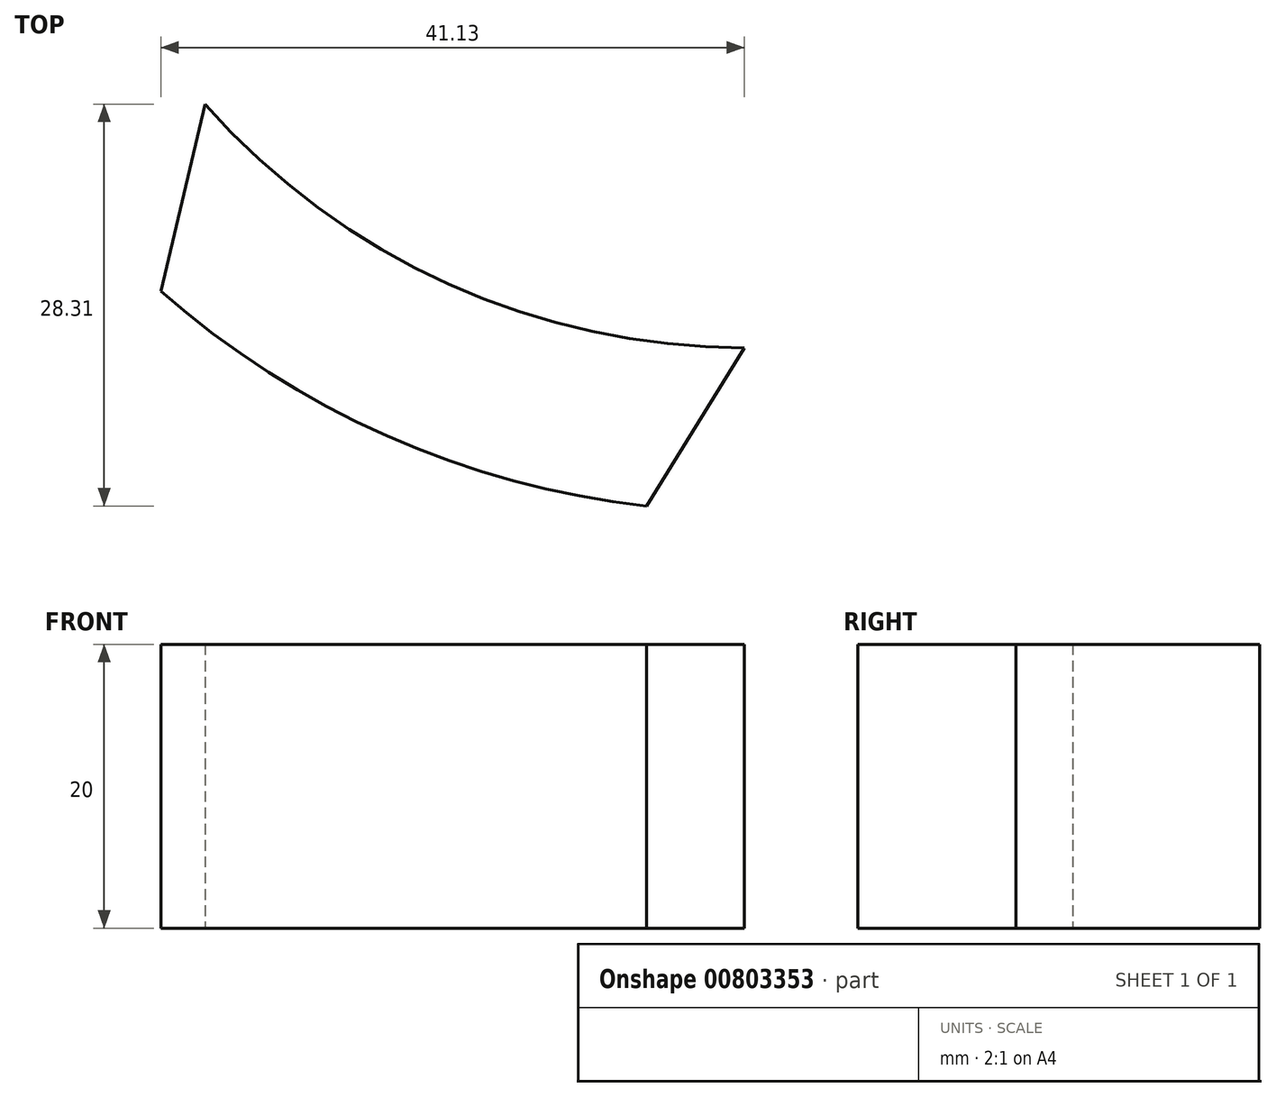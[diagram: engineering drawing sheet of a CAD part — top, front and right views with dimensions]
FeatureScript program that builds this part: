
annotation { "Feature Type Name" : "Feature", "Feature Type Description" : "" }
export const myFeature = defineFeature(function(context is Context, id is Id, definition is map)
    precondition{}
    {
        {
            var Q0;
            Q0=qCreatedBy(makeId("Top.planeOp"),FACE);
            var sketch = newSketch(context, id + "F0", { "sketchPlane" : qUnion([Q0])});
            skArc(sketch, "E0", {"start": v(-38.01, -33.51) * mm, "mid": v(-20.85, -46.19) * mm, "end": v(0, -50.68) * mm});
            skArc(sketch, "E1", {"start": v(-41.13, -46.67) * mm, "mid": v(-25.19, -56.88) * mm, "end": v(-6.9, -61.82) * mm});
            skLineSegment(sketch, "E2", {"start": v(-38.01, -33.51) * mm, "end": v(-41.13, -46.67) * mm});
            skLineSegment(sketch, "E3", {"start": v(0, -50.68) * mm, "end": v(-6.9, -61.82) * mm});
            skSolve(sketch);
        }
        {
            var Q0;
            Q0=makeQuery(id+"F0.imprint","IMPRINT",FACE,{"disambiguationData":[TD([[makeQuery(id+"F0.imprint","IMPRINT",EDGE,{"derivedFrom":sQuery(id+"F0.wireOp",EDGE,"E0")}),-1.0]])]});
            extrude(context, id + "F1", {"entities" : qUnion([Q0]), "depth" : 20 * mm, "offsetDistance" : 25 * mm});
        }
    });
